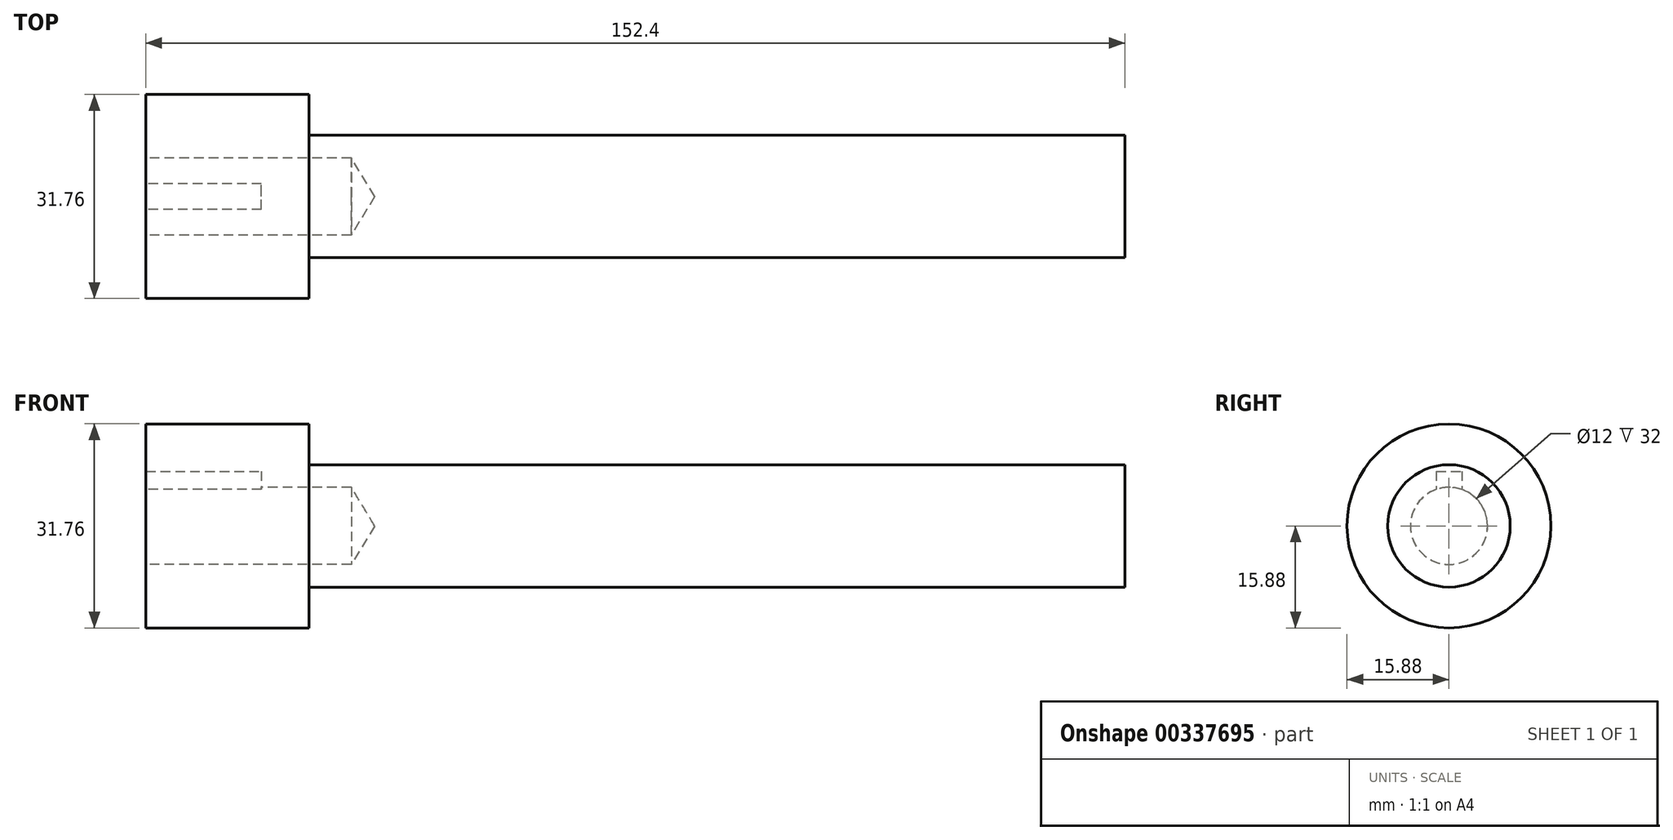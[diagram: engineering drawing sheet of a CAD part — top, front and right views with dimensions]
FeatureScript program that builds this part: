
annotation { "Feature Type Name" : "Feature", "Feature Type Description" : "" }
export const myFeature = defineFeature(function(context is Context, id is Id, definition is map)
    precondition{}
    {
        {
            var Q0;
            Q0=qCreatedBy(makeId("Right.planeOp"),FACE);
            var sketch = newSketch(context, id + "F0", { "sketchPlane" : qUnion([Q0])});
            skCircle(sketch, "E0", {"center": v(0, 0) * mm, "radius": 15.88 * mm});
            skSolve(sketch);
        }
        {
            var Q0;
            Q0=makeQuery(id+"F0.imprint","IMPRINT",FACE,{"disambiguationData":[TD([[makeQuery(id+"F0.imprint","IMPRINT",EDGE,{"derivedFrom":sQuery(id+"F0.wireOp",EDGE,"E0")}),1.0]])]});
            extrude(context, id + "F1", {"entities" : qUnion([Q0]), "depth" : 152.4 * mm});
        }
        {
            var Q0;
            Q0=makeQuery(id+"F1.opExtrude","CAP_FACE",FACE,{"disambiguationData":[OSD([sQuery(id+"F0.wireOp",EDGE,"E0")])],"isStart":true});
            var sketch = newSketch(context, id + "F2", { "sketchPlane" : qUnion([Q0])});
            skPoint(sketch, "E1", {"position": v(0, 0) * mm});
            skSolve(sketch);
        }
        {
            var Q0;
            Q0=sQuery(id+"F2.wireOp",VERTEX,"E1");
            var Q1;
            Q1=makeQuery(id+"F1.opExtrude","SWEPT_BODY",BODY,{"disambiguationData":[OSD([sQuery(id+"F0.wireOp",EDGE,"E0")])]});
            hole(context, id + "F3", {"style" : HoleStyle.SIMPLE, "endStyle" : HoleEndStyle.BLIND, "holeDiameter" : 12 * mm, "holeDepth" : 32 * mm, "isTappedThrough" : true, "tappedDepth" : 12.7 * mm, "tapClearance" : 3, "locations" : qUnion([Q0]), "scope" : qUnion([Q1])});
        }
        {
            var Q0;
            Q0=qCreatedBy(makeId("Top.planeOp"),FACE);
            var sketch = newSketch(context, id + "F4", { "sketchPlane" : qUnion([Q0])});
            skLineSegment(sketch, "E2.bottom", {"start": v(0, -2) * mm, "end": v(18, -2) * mm});
            skLineSegment(sketch, "E2.top", {"start": v(0, 2) * mm, "end": v(18, 2) * mm});
            skLineSegment(sketch, "E2.left", {"start": v(0, -2) * mm, "end": v(0, 2) * mm});
            skLineSegment(sketch, "E2.right", {"start": v(18, -2) * mm, "end": v(18, 2) * mm});
            skSolve(sketch);
        }
        {
            var Q0;
            Q0 = qSketchRegion(id + "F4", true);
            extrude(context, id + "F5", {"entities" : qUnion([Q0]), "operationType" : NewBodyOperationType.REMOVE, "depth" : 8.5 * mm});
        }
        {
            var Q0;
            Q0=makeQuery(id+"F1.opExtrude","CAP_FACE",FACE,{"disambiguationData":[OSD([sQuery(id+"F0.wireOp",EDGE,"E0")])],"isStart":false});
            var sketch = newSketch(context, id + "F6", { "sketchPlane" : qUnion([Q0])});
            skCircle(sketch, "E3", {"center": v(0, 0) * mm, "radius": 15.88 * mm});
            skCircle(sketch, "E4", {"center": v(0, 0) * mm, "radius": 9.53 * mm});
            skSolve(sketch);
        }
        {
            var Q0;
            Q0 = qSketchRegion(id + "F6", true);
            extrude(context, id + "F7", {"entities" : qUnion([Q0]), "operationType" : NewBodyOperationType.REMOVE, "oppositeDirection" : true, "depth" : 127 * mm});
        }
    });
